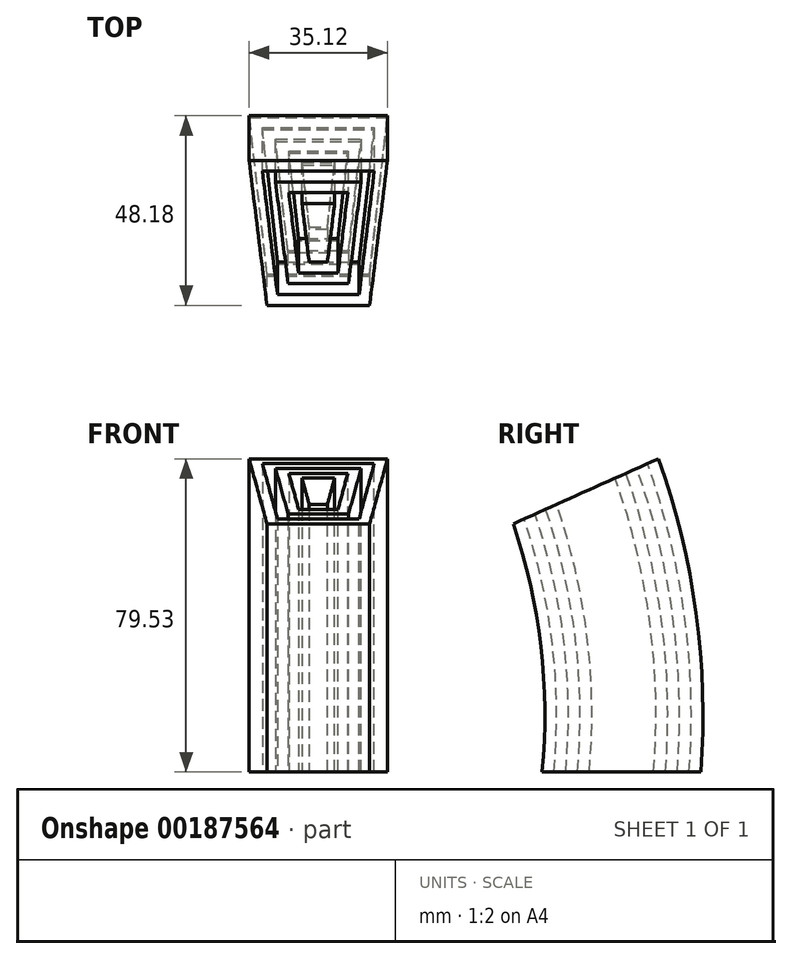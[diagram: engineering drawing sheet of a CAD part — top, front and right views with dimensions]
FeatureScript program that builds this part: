
annotation { "Feature Type Name" : "Feature", "Feature Type Description" : "" }
export const myFeature = defineFeature(function(context is Context, id is Id, definition is map)
    precondition{}
    {
        {
            var Q0;
            Q0=qCreatedBy(makeId("Top.planeOp"),FACE);
            var sketch = newSketch(context, id + "F0", { "sketchPlane" : qUnion([Q0])});
            skLineSegment(sketch, "E0", {"start": v(-6.46, 12.78) * mm, "end": v(8.54, 12.78) * mm});
            skLineSegment(sketch, "E1", {"start": v(8.54, 12.78) * mm, "end": v(6.04, -9.56) * mm});
            skLineSegment(sketch, "E2", {"start": v(6.04, -9.56) * mm, "end": v(-3.96, -9.56) * mm});
            skLineSegment(sketch, "E3", {"start": v(-3.96, -9.56) * mm, "end": v(-6.46, 12.78) * mm});
            skLineSegment(sketch, "E4.0", {"start": v(5.18, 9.78) * mm, "end": v(3.36, -6.56) * mm});
            skLineSegment(sketch, "E4.1", {"start": v(-3.1, 9.78) * mm, "end": v(5.18, 9.78) * mm});
            skLineSegment(sketch, "E4.2", {"start": v(-1.28, -6.56) * mm, "end": v(-3.1, 9.78) * mm});
            skLineSegment(sketch, "E4.3", {"start": v(3.36, -6.56) * mm, "end": v(-1.28, -6.56) * mm});
            skLineSegment(sketch, "E5.0", {"start": v(11.9, 15.78) * mm, "end": v(8.72, -12.56) * mm});
            skLineSegment(sketch, "E5.1", {"start": v(-9.82, 15.78) * mm, "end": v(11.9, 15.78) * mm});
            skLineSegment(sketch, "E5.2", {"start": v(-6.64, -12.56) * mm, "end": v(-9.82, 15.78) * mm});
            skLineSegment(sketch, "E5.3", {"start": v(8.72, -12.56) * mm, "end": v(-6.64, -12.56) * mm});
            skLineSegment(sketch, "E6.0", {"start": v(15.25, 18.78) * mm, "end": v(11.4, -15.56) * mm});
            skLineSegment(sketch, "E6.1", {"start": v(-13.17, 18.78) * mm, "end": v(15.25, 18.78) * mm});
            skLineSegment(sketch, "E6.2", {"start": v(-9.33, -15.56) * mm, "end": v(-13.17, 18.78) * mm});
            skLineSegment(sketch, "E6.3", {"start": v(11.4, -15.56) * mm, "end": v(-9.33, -15.56) * mm});
            skLineSegment(sketch, "E7.0", {"start": v(18.6, 21.78) * mm, "end": v(14.09, -18.56) * mm});
            skLineSegment(sketch, "E7.1", {"start": v(-16.52, 21.78) * mm, "end": v(18.6, 21.78) * mm});
            skLineSegment(sketch, "E7.2", {"start": v(-12, -18.56) * mm, "end": v(-16.52, 21.78) * mm});
            skLineSegment(sketch, "E7.3", {"start": v(14.09, -18.56) * mm, "end": v(-12, -18.56) * mm});
            skSolve(sketch);
        }
        {
            var Q0;
            Q0=qCreatedBy(makeId("Right.planeOp"),FACE);
            var sketch = newSketch(context, id + "F1", { "sketchPlane" : qUnion([Q0])});
            skLineSegment(sketch, "E8.0", {"start": v(9.78, 0) * mm, "end": v(-6.56, 0) * mm});
            skLineSegment(sketch, "E9.0", {"start": v(12.78, 0) * mm, "end": v(-9.56, 0) * mm});
            skLineSegment(sketch, "E10.0", {"start": v(15.78, 0) * mm, "end": v(-12.56, 0) * mm});
            skLineSegment(sketch, "E11.0", {"start": v(18.78, 0) * mm, "end": v(-15.56, 0) * mm});
            skLineSegment(sketch, "E12.0", {"start": v(21.78, 0) * mm, "end": v(-18.56, 0) * mm});
            skArc(sketch, "E13", {"start": v(9.78, 0) * mm, "mid": v(8.83, 37.83) * mm, "end": v(0, 74.63) * mm});
            skLineSegment(sketch, "E14", {"start": v(0, 74.63) * mm, "end": v(-42.65, 74.63) * mm});
            skLineSegment(sketch, "E15", {"start": v(-42.65, 74.63) * mm, "end": v(75.23, 74.63) * mm});
            skSolve(sketch);
        }
        {
            var Q0;
            Q0=makeQuery(id+"F0.imprint","IMPRINT",FACE,{"disambiguationData":[TD([[makeQuery(id+"F0.imprint","IMPRINT",EDGE,{"derivedFrom":sQuery(id+"F0.wireOp",EDGE,"E4.0")}),-1.0]])]});
            var Q1;
            Q1=makeQuery(id+"F0.imprint","IMPRINT",FACE,{"disambiguationData":[TD([[makeQuery(id+"F0.imprint","IMPRINT",EDGE,{"derivedFrom":sQuery(id+"F0.wireOp",EDGE,"E0")}),1.0]])]});
            var Q2;
            Q2=makeQuery(id+"F0.imprint","IMPRINT",FACE,{"disambiguationData":[TD([[makeQuery(id+"F0.imprint","IMPRINT",EDGE,{"derivedFrom":sQuery(id+"F0.wireOp",EDGE,"E6.0")}),1.0]])]});
            var Q3;
            Q3=sQuery(id+"F1.wireOp",EDGE,"E13");
            sweep(context, id + "F2", {"profiles" : qUnion([Q0, Q1, Q2]), "path" : qUnion([Q3])});
        }
    });
